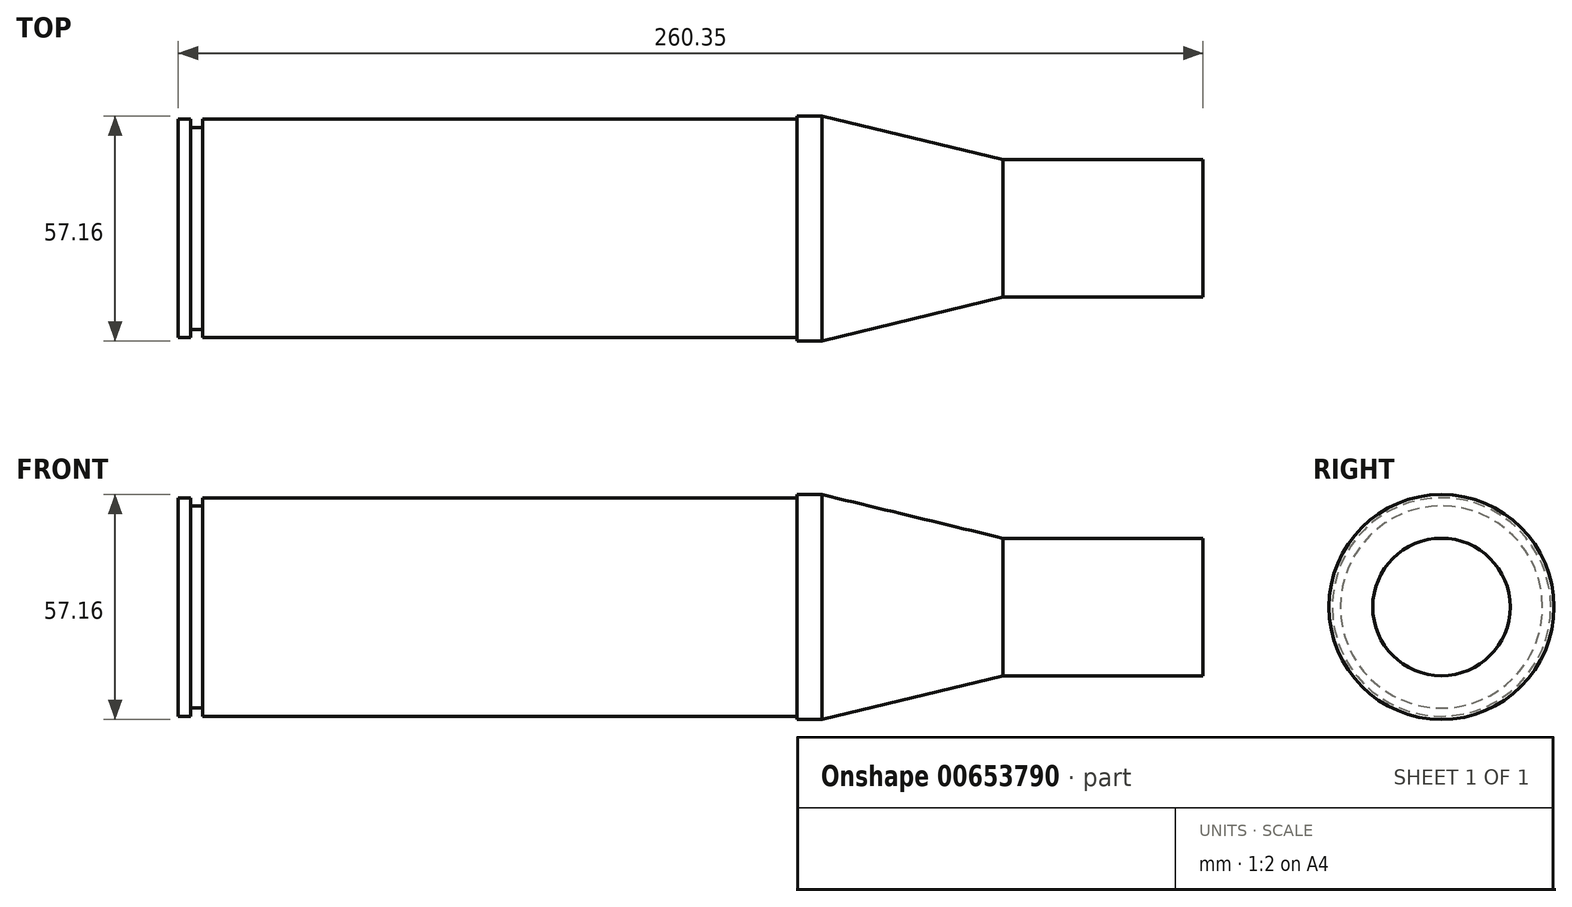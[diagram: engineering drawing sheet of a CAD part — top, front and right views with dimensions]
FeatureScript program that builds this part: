
annotation { "Feature Type Name" : "Feature", "Feature Type Description" : "" }
export const myFeature = defineFeature(function(context is Context, id is Id, definition is map)
    precondition{}
    {
        {
            var Q0;
            Q0=qCreatedBy(makeId("Front.planeOp"),FACE);
            var sketch = newSketch(context, id + "F0", { "sketchPlane" : qUnion([Q0])});
            skLineSegment(sketch, "E0", {"start": v(-157.18, 0) * mm, "end": v(-157.18, 27.75) * mm});
            skLineSegment(sketch, "E1", {"start": v(-157.18, 27.75) * mm, "end": v(-153.99, 27.75) * mm});
            skLineSegment(sketch, "E2", {"start": v(0, 27.75) * mm, "end": v(0, 28.58) * mm});
            skLineSegment(sketch, "E3", {"start": v(0, 28.58) * mm, "end": v(6.35, 28.58) * mm});
            skLineSegment(sketch, "E4", {"start": v(6.35, 28.58) * mm, "end": v(52.37, 17.46) * mm});
            skLineSegment(sketch, "E5", {"start": v(52.37, 17.46) * mm, "end": v(103.17, 17.46) * mm});
            skLineSegment(sketch, "E6", {"start": v(103.17, 17.46) * mm, "end": v(103.17, 0) * mm});
            skLineSegment(sketch, "E7", {"start": v(-153.99, 27.75) * mm, "end": v(-153.99, 25.68) * mm});
            skLineSegment(sketch, "E8", {"start": v(-153.99, 25.68) * mm, "end": v(-151, 25.68) * mm});
            skLineSegment(sketch, "E9", {"start": v(-151, 25.68) * mm, "end": v(-151, 27.75) * mm});
            skLineSegment(sketch, "E10.trimOffspring", {"start": v(-151, 27.75) * mm, "end": v(0, 27.75) * mm});
            skLineSegment(sketch, "E11", {"start": v(-157.18, 0) * mm, "end": v(103.17, 0) * mm});
            skSolve(sketch);
        }
        {
            var Q0;
            Q0=qSketchRegion(id+"F0",true);
            var Q1;
            Q1=sQuery(id+"F0.wireOp",EDGE,"E11");
            revolve(context, id + "F1", {"entities" : qUnion([Q0]), "axis" : qUnion([Q1]), "revolveType" : RevolveType.FULL});
        }
    });
